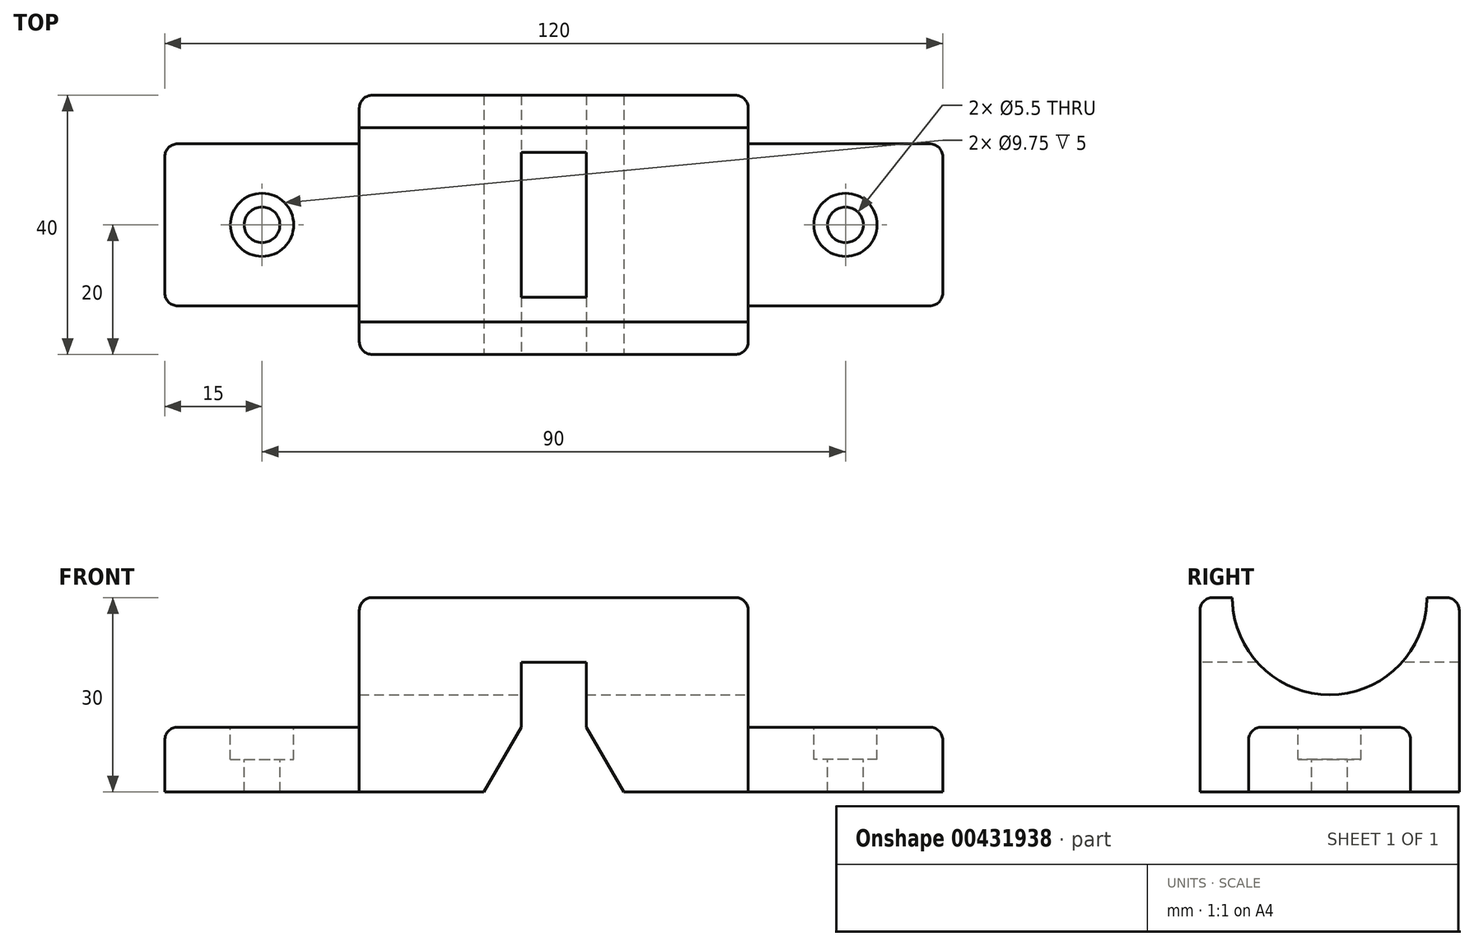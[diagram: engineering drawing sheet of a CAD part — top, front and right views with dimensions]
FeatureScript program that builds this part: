
annotation { "Feature Type Name" : "Feature", "Feature Type Description" : "" }
export const myFeature = defineFeature(function(context is Context, id is Id, definition is map)
    precondition{}
    {
        {
            var Q0;
            Q0=qCreatedBy(makeId("Top.planeOp"),FACE);
            var sketch = newSketch(context, id + "F0", { "sketchPlane" : qUnion([Q0])});
            skLineSegment(sketch, "E0.bottom", {"start": v(-30, 20) * mm, "end": v(30, 20) * mm});
            skLineSegment(sketch, "E0.top", {"start": v(-30, -20) * mm, "end": v(30, -20) * mm});
            skLineSegment(sketch, "E0.left", {"start": v(-30, 20) * mm, "end": v(-30, -20) * mm});
            skLineSegment(sketch, "E0.right", {"start": v(30, 20) * mm, "end": v(30, -20) * mm});
            skSolve(sketch);
        }
        {
            var Q0;
            Q0=makeQuery(id+"F0.imprint","IMPRINT",FACE,{"disambiguationData":[TD([[makeQuery(id+"F0.imprint","IMPRINT",EDGE,{"derivedFrom":sQuery(id+"F0.wireOp",EDGE,"E0.bottom")}),-1.0]])]});
            extrude(context, id + "F1", {"entities" : qUnion([Q0]), "depth" : 30 * mm});
        }
        {
            var Q0;
            Q0=makeQuery(id+"F1.opExtrude","SWEPT_FACE",FACE,{"disambiguationData":[OSD([sQuery(id+"F0.wireOp",EDGE,"E0.top")])]});
            var sketch = newSketch(context, id + "F2", { "sketchPlane" : qUnion([Q0])});
            skLineSegment(sketch, "E1", {"start": v(-10.77, 0) * mm, "end": v(-5, 10) * mm});
            skLineSegment(sketch, "E2", {"start": v(-5, 10) * mm, "end": v(-5, 20) * mm});
            skLineSegment(sketch, "E3", {"start": v(-5, 20) * mm, "end": v(5, 20) * mm});
            skLineSegment(sketch, "E4", {"start": v(5, 20) * mm, "end": v(5, 10) * mm});
            skLineSegment(sketch, "E5", {"start": v(5, 10) * mm, "end": v(10.77, 0) * mm});
            skLineSegment(sketch, "E6", {"start": v(-10.77, 0) * mm, "end": v(10.77, 0) * mm});
            skSolve(sketch);
        }
        {
            var Q0;
            Q0=makeQuery(id+"F2.imprint","IMPRINT",FACE,{"disambiguationData":[TD([[makeQuery(id+"F2.imprint","IMPRINT",EDGE,{"derivedFrom":sQuery(id+"F2.wireOp",EDGE,"E1")}),-1.0]])]});
            extrude(context, id + "F3", {"entities" : qUnion([Q0]), "operationType" : NewBodyOperationType.REMOVE, "endBound" : BoundingType.THROUGH_ALL, "oppositeDirection" : true, "depth" : 25 * mm});
        }
        {
            var Q0;
            Q0=qCreatedBy(makeId("Right.planeOp"),FACE);
            var sketch = newSketch(context, id + "F4", { "sketchPlane" : qUnion([Q0])});
            skCircle(sketch, "E7", {"center": v(0, 30) * mm, "radius": 15 * mm});
            skSolve(sketch);
        }
        {
            var Q0;
            Q0=makeQuery(id+"F4.imprint","IMPRINT",FACE,{"disambiguationData":[TD([[makeQuery(id+"F4.imprint","IMPRINT",EDGE,{"derivedFrom":sQuery(id+"F4.wireOp",EDGE,"E7")}),1.0]])]});
            extrude(context, id + "F5", {"entities" : qUnion([Q0]), "operationType" : NewBodyOperationType.REMOVE, "endBound" : BoundingType.SYMMETRIC, "oppositeDirection" : true, "depth" : 80 * mm});
        }
        {
            var Q0;
            Q0=makeQuery(id+"F1.opExtrude","SWEPT_FACE",FACE,{"disambiguationData":[OSD([sQuery(id+"F0.wireOp",EDGE,"E0.right")])]});
            var sketch = newSketch(context, id + "F6", { "sketchPlane" : qUnion([Q0])});
            skLineSegment(sketch, "E8.bottom", {"start": v(-12.5, 0) * mm, "end": v(12.5, 0) * mm});
            skLineSegment(sketch, "E8.top", {"start": v(-12.5, 10) * mm, "end": v(12.5, 10) * mm});
            skLineSegment(sketch, "E8.left", {"start": v(-12.5, 0) * mm, "end": v(-12.5, 10) * mm});
            skLineSegment(sketch, "E8.right", {"start": v(12.5, 0) * mm, "end": v(12.5, 10) * mm});
            skSolve(sketch);
        }
        {
            var Q0;
            Q0=makeQuery(id+"F6.imprint","IMPRINT",FACE,{"disambiguationData":[TD([[makeQuery(id+"F6.imprint","IMPRINT",EDGE,{"derivedFrom":sQuery(id+"F6.wireOp",EDGE,"E8.bottom")}),-1.0]])]});
            extrude(context, id + "F7", {"entities" : qUnion([Q0]), "operationType" : NewBodyOperationType.ADD, "depth" : 30 * mm});
        }
        {
            var Q0;
            Q0=makeQuery(id+"F7.opExtrude","SWEPT_FACE",FACE,{"disambiguationData":[OSD([sQuery(id+"F6.wireOp",EDGE,"E8.top")])]});
            var sketch = newSketch(context, id + "F8", { "sketchPlane" : qUnion([Q0])});
            skPoint(sketch, "E9", {"position": v(45, 0) * mm});
            skPoint(sketch, "E9.positionSnap0", {"position": v(45, 12.5) * mm});
            skPoint(sketch, "E9.positionSnap1", {"position": v(60, 0) * mm});
            skSolve(sketch);
        }
        {
            var Q0;
            Q0=sQuery(id+"F8.wireOp",VERTEX,"E9");
            var Q1;
            Q1=makeQuery(id+"F1.opExtrude","SWEPT_BODY",BODY,{"disambiguationData":[OSD([sQuery(id+"F0.wireOp",EDGE,"E0.bottom"),sQuery(id+"F0.wireOp",EDGE,"E0.top"),sQuery(id+"F0.wireOp",EDGE,"E0.left"),sQuery(id+"F0.wireOp",EDGE,"E0.right")])]});
            hole(context, id + "F9", {"style" : HoleStyle.C_BORE, "endStyle" : HoleEndStyle.THROUGH, "standardTappedOrClearance" : lookupTablePath({ "standard" : "ISO", "fit" : "Normal", "size" : "M5", "type" : "Clearance" }), "standardBlindInLast" : lookupTablePath({ "fit" : "Standard", "standard" : "ISO", "size" : "M5", "type" : "Clearance" }), "holeDiameter" : 5.5 * mm, "cBoreDiameter" : 9.75 * mm, "cBoreDepth" : 5 * mm, "isTappedThrough" : true, "tappedDepth" : 7.24 * mm, "tapClearance" : 3, "locations" : qUnion([Q0]), "scope" : qUnion([Q1])});
        }
        {
            var Q0;
            Q0=makeQuery(id+"F7.opExtrude","CAP_EDGE",EDGE,{"disambiguationData":[OSD([sQuery(id+"F6.wireOp",EDGE,"E8.left")])],"isStart":false});
            var Q1;
            Q1=makeQuery(id+"F7.opExtrude","CAP_EDGE",EDGE,{"disambiguationData":[OSD([sQuery(id+"F6.wireOp",EDGE,"E8.right")])],"isStart":false});
            var Q2;
            Q2=makeQuery(id+"F7.opExtrude","SWEPT_EDGE",EDGE,{"disambiguationData":[OSD([sQuery(id+"F6.wireOp",EDGE,"E8.top"),sQuery(id+"F6.wireOp",EDGE,"E8.left")])]});
            var Q3;
            Q3=makeQuery(id+"F7.opExtrude","CAP_EDGE",EDGE,{"disambiguationData":[OSD([sQuery(id+"F6.wireOp",EDGE,"E8.top")])],"isStart":false});
            var Q4;
            Q4=makeQuery(id+"F7.opExtrude","SWEPT_EDGE",EDGE,{"disambiguationData":[OSD([sQuery(id+"F6.wireOp",EDGE,"E8.top"),sQuery(id+"F6.wireOp",EDGE,"E8.right")])]});
            var Q5;
            Q5=makeQuery(id+"F7.opExtrude","CAP_EDGE",EDGE,{"disambiguationData":[OSD([sQuery(id+"F6.wireOp",EDGE,"E8.left")])],"isStart":true});
            var Q6;
            Q6=makeQuery(id+"F1.opExtrude","SWEPT_EDGE",EDGE,{"disambiguationData":[OSD([sQuery(id+"F0.wireOp",EDGE,"E0.top"),sQuery(id+"F0.wireOp",EDGE,"E0.right")])]});
            var Q7;
            {var subQ0=sQuery(id+"F0.wireOp",EDGE,"E0.right");var subQ1=sQuery(id+"F0.wireOp",EDGE,"E0.top");Q7=makeQuery(id+"F5.boolean.opBoolean","SPLIT",EDGE,{"disambiguationData":[TD([makeQuery(id+"F1.opExtrude","SWEPT_FACE",FACE,{"disambiguationData":[OSD([subQ1])]})])],"derivedFrom":makeQuery(id+"F1.opExtrude","CAP_EDGE",EDGE,{"disambiguationData":[OSD([subQ0])],"isStart":false})});}
            var Q8;
            {var subQ0=sQuery(id+"F0.wireOp",EDGE,"E0.left");var subQ1=sQuery(id+"F0.wireOp",EDGE,"E0.top");Q8=makeQuery(id+"F5.boolean.opBoolean","SPLIT",EDGE,{"disambiguationData":[TD([makeQuery(id+"F1.opExtrude","SWEPT_FACE",FACE,{"disambiguationData":[OSD([subQ1])]})])],"derivedFrom":makeQuery(id+"F1.opExtrude","CAP_EDGE",EDGE,{"disambiguationData":[OSD([subQ0])],"isStart":false})});}
            var Q9;
            Q9=makeQuery(id+"F1.opExtrude","SWEPT_EDGE",EDGE,{"disambiguationData":[OSD([sQuery(id+"F0.wireOp",EDGE,"E0.bottom"),sQuery(id+"F0.wireOp",EDGE,"E0.right")])]});
            var Q10;
            Q10=makeQuery(id+"F1.opExtrude","CAP_EDGE",EDGE,{"disambiguationData":[OSD([sQuery(id+"F0.wireOp",EDGE,"E0.bottom")])],"isStart":false});
            var Q11;
            {var subQ0=sQuery(id+"F0.wireOp",EDGE,"E0.bottom");var subQ1=sQuery(id+"F0.wireOp",EDGE,"E0.left");Q11=makeQuery(id+"F5.boolean.opBoolean","SPLIT",EDGE,{"disambiguationData":[TD([makeQuery(id+"F1.opExtrude","SWEPT_FACE",FACE,{"disambiguationData":[OSD([subQ0])]})])],"derivedFrom":makeQuery(id+"F1.opExtrude","CAP_EDGE",EDGE,{"disambiguationData":[OSD([subQ1])],"isStart":false})});}
            var Q12;
            Q12=makeQuery(id+"F1.opExtrude","SWEPT_EDGE",EDGE,{"disambiguationData":[OSD([sQuery(id+"F0.wireOp",EDGE,"E0.top"),sQuery(id+"F0.wireOp",EDGE,"E0.left")])]});
            var Q13;
            Q13=makeQuery(id+"F1.opExtrude","SWEPT_EDGE",EDGE,{"disambiguationData":[OSD([sQuery(id+"F0.wireOp",EDGE,"E0.bottom"),sQuery(id+"F0.wireOp",EDGE,"E0.left")])]});
            var Q14;
            Q14=makeQuery(id+"F1.opExtrude","CAP_EDGE",EDGE,{"disambiguationData":[OSD([sQuery(id+"F0.wireOp",EDGE,"E0.top")])],"isStart":false});
            var Q15;
            {var subQ0=sQuery(id+"F0.wireOp",EDGE,"E0.bottom");var subQ1=sQuery(id+"F0.wireOp",EDGE,"E0.right");Q15=makeQuery(id+"F5.boolean.opBoolean","SPLIT",EDGE,{"disambiguationData":[TD([makeQuery(id+"F1.opExtrude","SWEPT_FACE",FACE,{"disambiguationData":[OSD([subQ0])]})])],"derivedFrom":makeQuery(id+"F1.opExtrude","CAP_EDGE",EDGE,{"disambiguationData":[OSD([subQ1])],"isStart":false})});}
            fillet(context, id + "F10", {"entities" : qUnion([Q0, Q1, Q2, Q3, Q4, Q5, Q6, Q7, Q8, Q9, Q10, Q11, Q12, Q13, Q14, Q15]), "radius" : 2 * mm, "tangentPropagation" : true, "allowEdgeOverflow" : false});
        }
        {
            var Q0;
            Q0=makeQuery(id+"F1.opExtrude","SWEPT_BODY",BODY,{"disambiguationData":[OSD([sQuery(id+"F0.wireOp",EDGE,"E0.bottom"),sQuery(id+"F0.wireOp",EDGE,"E0.top"),sQuery(id+"F0.wireOp",EDGE,"E0.left"),sQuery(id+"F0.wireOp",EDGE,"E0.right")])]});
            var Q1;
            Q1=qCreatedBy(makeId("Right.planeOp"),FACE);
            mirror(context, id + "F11", {"operationType" : NewBodyOperationType.ADD, "entities" : qUnion([Q0]), "mirrorPlane" : qUnion([Q1])});
        }
    });
